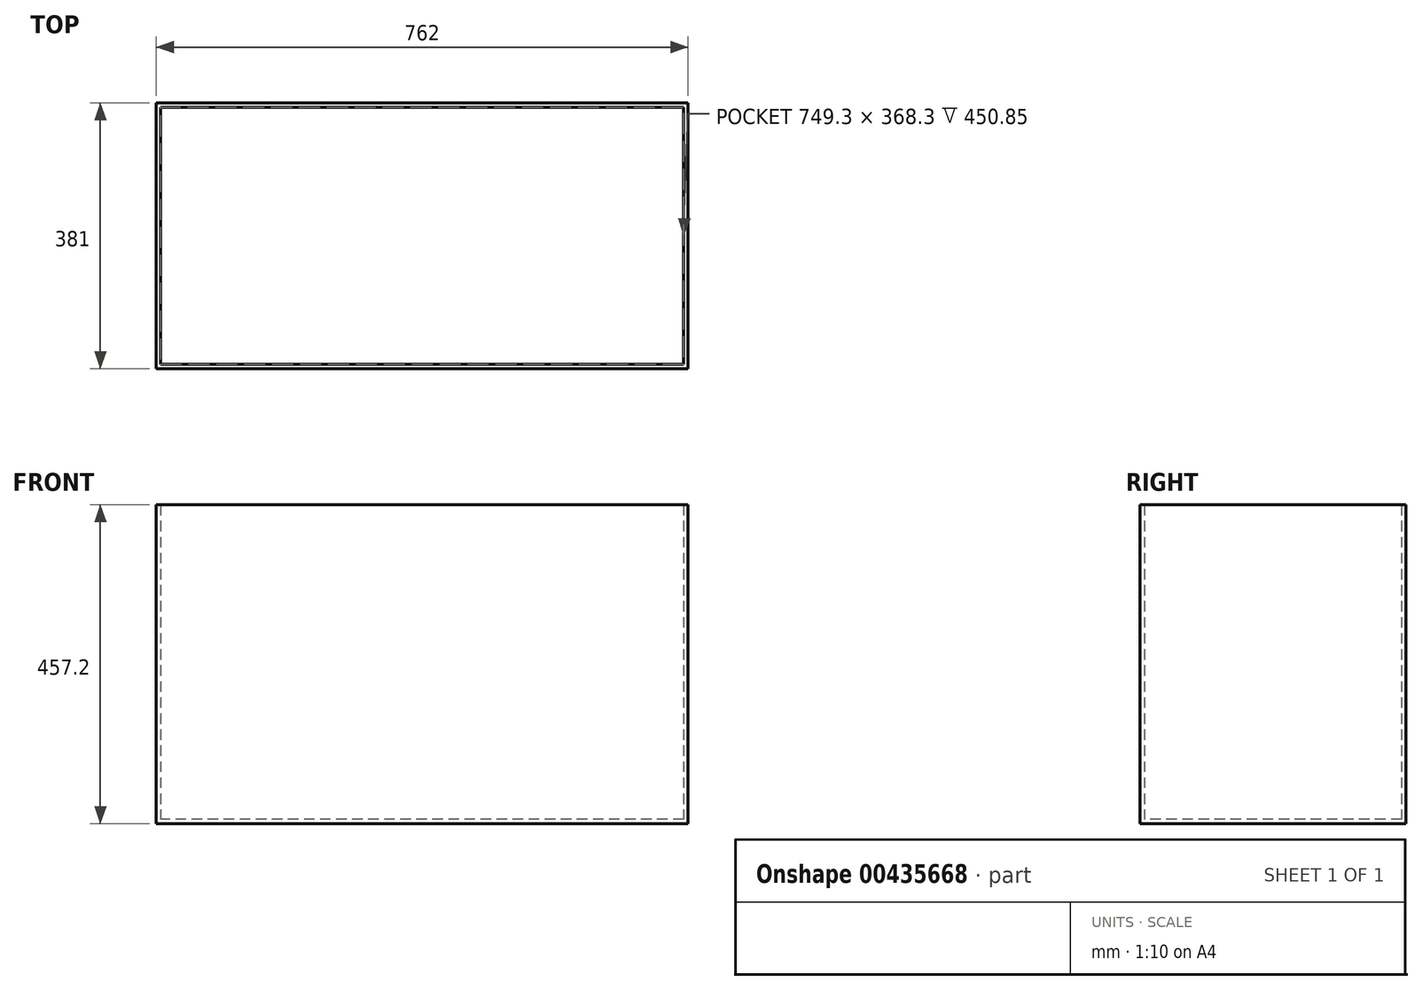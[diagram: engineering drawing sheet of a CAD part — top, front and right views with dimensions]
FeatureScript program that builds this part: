
annotation { "Feature Type Name" : "Feature", "Feature Type Description" : "" }
export const myFeature = defineFeature(function(context is Context, id is Id, definition is map)
    precondition{}
    {
        {
            var Q0;
            Q0=qCreatedBy(makeId("Top.planeOp"),FACE);
            var sketch = newSketch(context, id + "F0", { "sketchPlane" : qUnion([Q0])});
            skLineSegment(sketch, "E0.bottom", {"start": v(0, 0) * mm, "end": v(-762, 0) * mm});
            skLineSegment(sketch, "E0.top", {"start": v(0, -381) * mm, "end": v(-762, -381) * mm});
            skLineSegment(sketch, "E0.left", {"start": v(0, 0) * mm, "end": v(0, -381) * mm});
            skLineSegment(sketch, "E0.right", {"start": v(-762, 0) * mm, "end": v(-762, -381) * mm});
            skSolve(sketch);
        }
        {
            var Q0;
            Q0=makeQuery(id+"F0.imprint","IMPRINT",FACE,{"disambiguationData":[TD([[makeQuery(id+"F0.imprint","IMPRINT",EDGE,{"derivedFrom":sQuery(id+"F0.wireOp",EDGE,"E0.bottom")}),1.0]])]});
            extrude(context, id + "F1", {"entities" : qUnion([Q0]), "depth" : 431.8 * mm});
        }
        {
            var Q0;
            Q0=makeQuery(id+"F1.opExtrude","CAP_FACE",FACE,{"disambiguationData":[OSD([sQuery(id+"F0.wireOp",EDGE,"E0.bottom"),sQuery(id+"F0.wireOp",EDGE,"E0.top"),sQuery(id+"F0.wireOp",EDGE,"E0.left"),sQuery(id+"F0.wireOp",EDGE,"E0.right")])],"isStart":false});
            extrude(context, id + "F2", {"entities" : qUnion([Q0]), "operationType" : NewBodyOperationType.ADD, "depth" : 25.4 * mm});
        }
        {
            var Q0;
            Q0=makeQuery(id+"F2.opExtrude","CAP_FACE",FACE,{"disambiguationData":[OSD([sQuery(id+"F0.wireOp",EDGE,"E0.bottom"),sQuery(id+"F0.wireOp",EDGE,"E0.top"),sQuery(id+"F0.wireOp",EDGE,"E0.left"),sQuery(id+"F0.wireOp",EDGE,"E0.right")])],"isStart":false});
            shell(context, id + "F3", {"entities" : qUnion([Q0]), "thickness" : 6.35 * mm});
        }
    });
